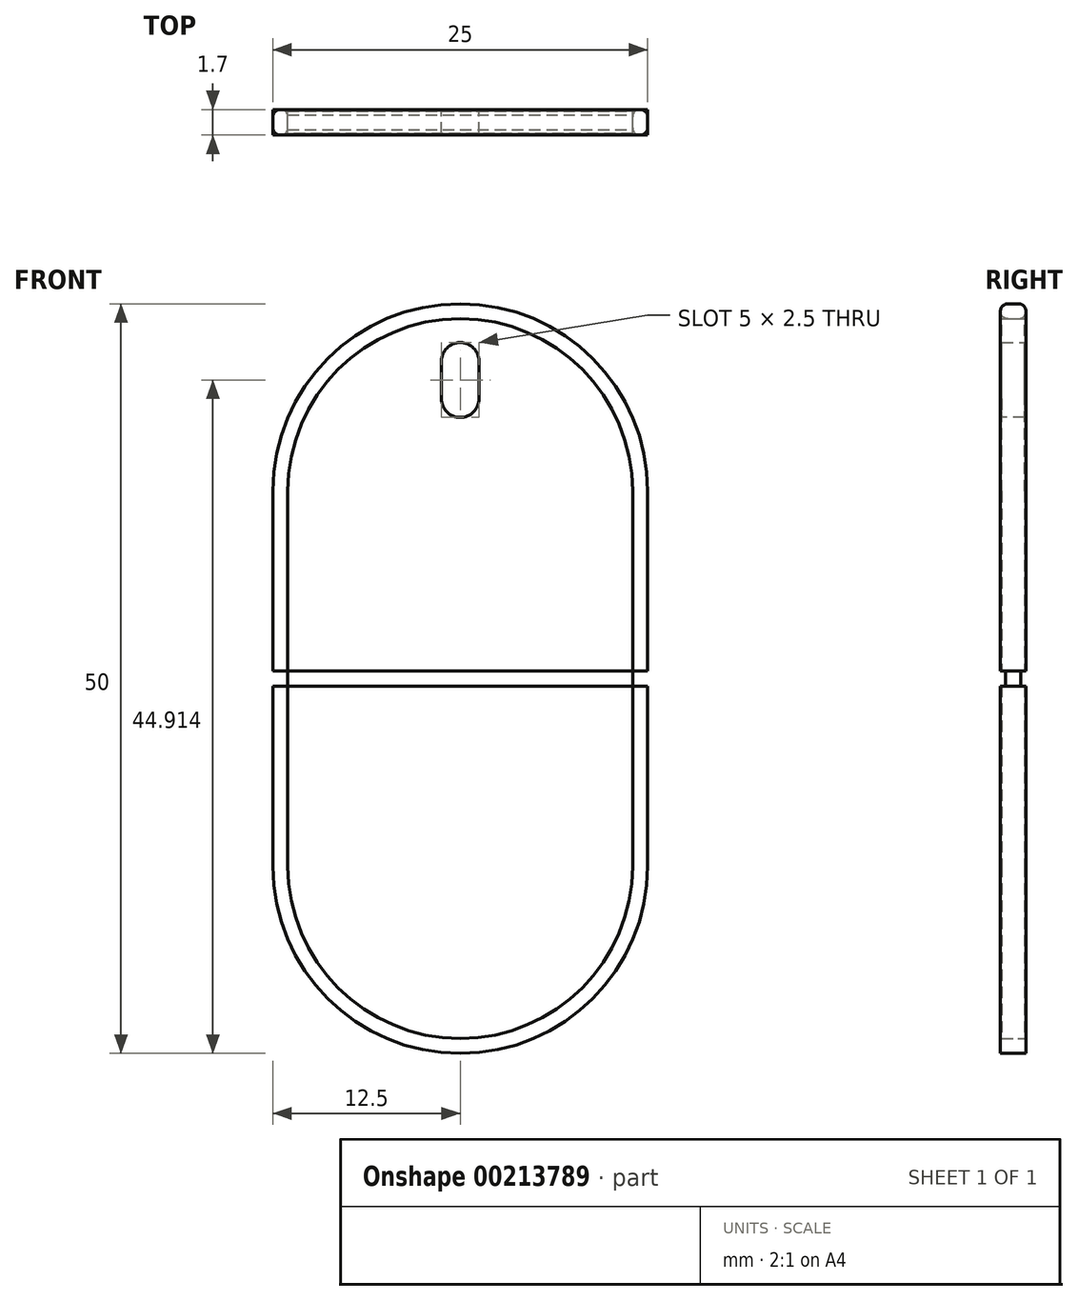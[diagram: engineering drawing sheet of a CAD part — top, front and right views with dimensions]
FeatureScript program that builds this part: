
annotation { "Feature Type Name" : "Feature", "Feature Type Description" : "" }
export const myFeature = defineFeature(function(context is Context, id is Id, definition is map)
    precondition{}
    {
        {
            var Q0;
            Q0=qCreatedBy(makeId("Front.planeOp"),FACE);
            var sketch = newSketch(context, id + "F0", { "sketchPlane" : qUnion([Q0])});
            skLineSegment(sketch, "E0.bottom", {"start": v(12.5, 25) * mm, "end": v(-12.5, 25) * mm});
            skLineSegment(sketch, "E0.top", {"start": v(12.5, -25) * mm, "end": v(-12.5, -25) * mm});
            skLineSegment(sketch, "E0.left", {"start": v(12.5, 25) * mm, "end": v(12.5, -25) * mm});
            skLineSegment(sketch, "E0.right", {"start": v(-12.5, 25) * mm, "end": v(-12.5, -25) * mm});
            skPoint(sketch, "E0.middle", {"position": v(0, 0) * mm});
            skLineSegment(sketch, "E1", {"start": v(-12.5, 0) * mm, "end": v(12.5, 0) * mm, "construction": true});
            skLineSegment(sketch, "E2.0", {"start": v(-12.5, 0.5) * mm, "end": v(12.5, 0.5) * mm});
            skLineSegment(sketch, "E3.MirrorCS", {"start": v(-12.5, -0.5) * mm, "end": v(12.5, -0.5) * mm});
            skLineSegment(sketch, "E4", {"start": v(11.5, 0.5) * mm, "end": v(11.5, -0.5) * mm});
            skLineSegment(sketch, "E5.MirrorCS", {"start": v(-11.5, 0.5) * mm, "end": v(-11.5, -0.5) * mm});
            skLineSegment(sketch, "E6.bottom", {"start": v(1.25, 17.41) * mm, "end": v(-1.25, 17.41) * mm});
            skLineSegment(sketch, "E6.top", {"start": v(1.25, 22.41) * mm, "end": v(-1.25, 22.41) * mm});
            skLineSegment(sketch, "E6.left", {"start": v(1.25, 17.41) * mm, "end": v(1.25, 22.41) * mm});
            skLineSegment(sketch, "E6.right", {"start": v(-1.25, 17.41) * mm, "end": v(-1.25, 22.41) * mm});
            skPoint(sketch, "E6.middle", {"position": v(0, 19.91) * mm});
            skLineSegment(sketch, "E7.0", {"start": v(0, 24) * mm, "end": v(0, 24) * mm});
            skLineSegment(sketch, "E7.1", {"start": v(11.5, 12.5) * mm, "end": v(11.5, -12.5) * mm});
            skLineSegment(sketch, "E7.2", {"start": v(0, -24) * mm, "end": v(0, -24) * mm});
            skLineSegment(sketch, "E7.3", {"start": v(-11.5, 12.5) * mm, "end": v(-11.5, -12.5) * mm});
            skPoint(sketch, "E8.visualSharp", {"position": v(11.5, 24) * mm});
            skArc(sketch, "E8.filletArc", {"start": v(11.5, 12.5) * mm, "mid": v(8.13, 20.63) * mm, "end": v(0, 24) * mm});
            skPoint(sketch, "E9.visualSharp", {"position": v(-11.5, 24) * mm});
            skArc(sketch, "E9.filletArc", {"start": v(0, 24) * mm, "mid": v(-8.13, 20.63) * mm, "end": v(-11.5, 12.5) * mm});
            skPoint(sketch, "E10.visualSharp", {"position": v(11.5, -24) * mm});
            skArc(sketch, "E10.filletArc", {"start": v(0, -24) * mm, "mid": v(8.13, -20.63) * mm, "end": v(11.5, -12.5) * mm});
            skPoint(sketch, "E11.visualSharp", {"position": v(-11.5, -24) * mm});
            skArc(sketch, "E11.filletArc", {"start": v(-11.5, -12.5) * mm, "mid": v(-8.13, -20.63) * mm, "end": v(0, -24) * mm});
            skSolve(sketch);
        }
        {
            var Q0;
            {var subQ7=sQuery(id+"F0.wireOp",EDGE,"E0.bottom");Q0=makeQuery(id+"F0.imprint","IMPRINT",FACE,{"disambiguationData":[TD([[makeQuery(id+"F0.imprint","IMPRINT",EDGE,{"derivedFrom":subQ7}),1.0]])]});}
            var Q1;
            {var subQ5=sQuery(id+"F0.wireOp",EDGE,"E0.top");Q1=makeQuery(id+"F0.imprint","IMPRINT",FACE,{"disambiguationData":[TD([[makeQuery(id+"F0.imprint","IMPRINT",EDGE,{"derivedFrom":subQ5}),-1.0]])]});}
            var Q2;
            {var subQ5=sQuery(id+"F0.wireOp",EDGE,"E7.2");Q2=makeQuery(id+"F0.imprint","IMPRINT",FACE,{"disambiguationData":[TD([[makeQuery(id+"F0.imprint","IMPRINT",EDGE,{"derivedFrom":subQ5}),-1.0]])]});}
            extrude(context, id + "F1", {"entities" : qUnion([Q0, Q1, Q2]), "depth" : .85 * mm, "hasSecondDirection" : true, "secondDirectionOppositeDirection" : true, "secondDirectionDepth" : .85 * mm});
        }
        {
            var Q0;
            Q0=makeQuery(id+"F1.opExtrude","SWEPT_EDGE",EDGE,{"disambiguationData":[OSD([sQuery(id+"F0.wireOp",EDGE,"E0.top"),sQuery(id+"F0.wireOp",EDGE,"E0.left")])]});
            var Q1;
            Q1=makeQuery(id+"F1.opExtrude","SWEPT_EDGE",EDGE,{"disambiguationData":[OSD([sQuery(id+"F0.wireOp",EDGE,"E0.top"),sQuery(id+"F0.wireOp",EDGE,"E0.right")])]});
            var Q2;
            Q2=makeQuery(id+"F1.opExtrude","SWEPT_EDGE",EDGE,{"disambiguationData":[OSD([sQuery(id+"F0.wireOp",EDGE,"E0.bottom"),sQuery(id+"F0.wireOp",EDGE,"E0.left")])]});
            var Q3;
            Q3=makeQuery(id+"F1.opExtrude","SWEPT_EDGE",EDGE,{"disambiguationData":[OSD([sQuery(id+"F0.wireOp",EDGE,"E0.bottom"),sQuery(id+"F0.wireOp",EDGE,"E0.right")])]});
            fillet(context, id + "F2", {"entities" : qUnion([Q0, Q1, Q2, Q3]), "radius" : 12.5 * mm, "tangentPropagation" : true, "allowEdgeOverflow" : false});
        }
        {
            var Q0;
            {var subQ4=sQuery(id+"F0.wireOp",EDGE,"E4");Q0=makeQuery(id+"F0.imprint","IMPRINT",FACE,{"disambiguationData":[TD([[makeQuery(id+"F0.imprint","IMPRINT",EDGE,{"derivedFrom":subQ4}),-1.0]])]});}
            extrude(context, id + "F3", {"entities" : qUnion([Q0]), "depth" : .5 * mm, "hasSecondDirection" : true, "secondDirectionOppositeDirection" : true, "secondDirectionDepth" : .5 * mm});
        }
        {
            var Q0;
            Q0=makeQuery(id+"F0.imprint","IMPRINT",FACE,{"disambiguationData":[TD([[makeQuery(id+"F0.imprint","IMPRINT",EDGE,{"derivedFrom":sQuery(id+"F0.wireOp",EDGE,"E6.bottom")}),1.0]])]});
            var Q1;
            {var subQ6=sQuery(id+"F0.wireOp",EDGE,"E10.filletArc");Q1=makeQuery(id+"F0.imprint","IMPRINT",FACE,{"disambiguationData":[TD([[makeQuery(id+"F0.imprint","IMPRINT",EDGE,{"derivedFrom":subQ6}),1.0]])]});}
            extrude(context, id + "F4", {"entities" : qUnion([Q0, Q1]), "depth" : .75 * mm, "hasSecondDirection" : true, "secondDirectionOppositeDirection" : true, "secondDirectionDepth" : .75 * mm});
        }
        {
            var Q0;
            Q0=makeQuery(id+"F4.opExtrude","SWEPT_EDGE",EDGE,{"disambiguationData":[OSD([sQuery(id+"F0.wireOp",EDGE,"E6.top"),sQuery(id+"F0.wireOp",EDGE,"E6.right")])]});
            var Q1;
            Q1=makeQuery(id+"F4.opExtrude","SWEPT_EDGE",EDGE,{"disambiguationData":[OSD([sQuery(id+"F0.wireOp",EDGE,"E6.top"),sQuery(id+"F0.wireOp",EDGE,"E6.left")])]});
            var Q2;
            Q2=makeQuery(id+"F4.opExtrude","SWEPT_EDGE",EDGE,{"disambiguationData":[OSD([sQuery(id+"F0.wireOp",EDGE,"E6.bottom"),sQuery(id+"F0.wireOp",EDGE,"E6.right")])]});
            var Q3;
            Q3=makeQuery(id+"F4.opExtrude","SWEPT_EDGE",EDGE,{"disambiguationData":[OSD([sQuery(id+"F0.wireOp",EDGE,"E6.bottom"),sQuery(id+"F0.wireOp",EDGE,"E6.left")])]});
            fillet(context, id + "F5", {"entities" : qUnion([Q0, Q1, Q2, Q3]), "radius" : 1.25 * mm, "tangentPropagation" : true, "allowEdgeOverflow" : false});
        }
        {
            var Q0;
            {var subQ0=sQuery(id+"F0.wireOp",EDGE,"E0.left");var subQ1=sQuery(id+"F0.wireOp",EDGE,"E0.bottom");Q0=makeQuery(id+"F2.opFillet","BLEND_EDGE",EDGE,{"blendedFrom":[makeQuery(id+"F1.opExtrude","SWEPT_EDGE",EDGE,{"disambiguationData":[OSD([subQ1,subQ0])]}),makeQuery(id+"F1.opExtrude","CAP_FACE",FACE,{"disambiguationData":[OSD([subQ1,subQ0,sQuery(id+"F0.wireOp",EDGE,"E0.right"),sQuery(id+"F0.wireOp",EDGE,"E2.0"),sQuery(id+"F0.wireOp",EDGE,"E7.1"),sQuery(id+"F0.wireOp",EDGE,"E7.3"),sQuery(id+"F0.wireOp",EDGE,"E8.filletArc"),sQuery(id+"F0.wireOp",EDGE,"E9.filletArc")])],"isStart":false})],"blendedInto":[makeQuery(id+"F1.opExtrude","CAP_FACE",FACE,{"disambiguationData":[OSD([subQ1,subQ0,sQuery(id+"F0.wireOp",EDGE,"E0.right"),sQuery(id+"F0.wireOp",EDGE,"E2.0"),sQuery(id+"F0.wireOp",EDGE,"E7.1"),sQuery(id+"F0.wireOp",EDGE,"E7.3"),sQuery(id+"F0.wireOp",EDGE,"E8.filletArc"),sQuery(id+"F0.wireOp",EDGE,"E9.filletArc")])],"isStart":false})]});}
            var Q1;
            {var subQ0=sQuery(id+"F0.wireOp",EDGE,"E0.left");Q1=makeQuery(id+"F1.opExtrude","CAP_EDGE",EDGE,{"disambiguationData":[OSD([subQ0]),TDD([makeQuery(id+"F0.imprint","IMPRINT",EDGE,{"disambiguationData":[TD([[makeQuery(id+"F0.imprint","INTERSECT",VERTEX,{"derivedFrom":[sQuery(id+"F0.wireOp",EDGE,"E0.bottom"),subQ0]}),-1.0]])],"derivedFrom":subQ0})])],"isStart":false});}
            var Q2;
            {var subQ0=sQuery(id+"F0.wireOp",EDGE,"E0.left");Q2=makeQuery(id+"F1.opExtrude","CAP_EDGE",EDGE,{"disambiguationData":[OSD([subQ0]),TDD([makeQuery(id+"F0.imprint","IMPRINT",EDGE,{"disambiguationData":[TD([[makeQuery(id+"F0.imprint","INTERSECT",VERTEX,{"derivedFrom":[sQuery(id+"F0.wireOp",EDGE,"E0.bottom"),subQ0]}),-1.0]])],"derivedFrom":subQ0})])],"isStart":true});}
            var Q3;
            {var subQ0=sQuery(id+"F0.wireOp",EDGE,"E0.left");var subQ1=sQuery(id+"F0.wireOp",EDGE,"E0.bottom");Q3=makeQuery(id+"F2.opFillet","BLEND_EDGE",EDGE,{"blendedFrom":[makeQuery(id+"F1.opExtrude","SWEPT_EDGE",EDGE,{"disambiguationData":[OSD([subQ1,subQ0])]}),makeQuery(id+"F1.opExtrude","CAP_FACE",FACE,{"disambiguationData":[OSD([subQ1,subQ0,sQuery(id+"F0.wireOp",EDGE,"E0.right"),sQuery(id+"F0.wireOp",EDGE,"E2.0"),sQuery(id+"F0.wireOp",EDGE,"E7.1"),sQuery(id+"F0.wireOp",EDGE,"E7.3"),sQuery(id+"F0.wireOp",EDGE,"E8.filletArc"),sQuery(id+"F0.wireOp",EDGE,"E9.filletArc")])],"isStart":true})],"blendedInto":[makeQuery(id+"F1.opExtrude","CAP_FACE",FACE,{"disambiguationData":[OSD([subQ1,subQ0,sQuery(id+"F0.wireOp",EDGE,"E0.right"),sQuery(id+"F0.wireOp",EDGE,"E2.0"),sQuery(id+"F0.wireOp",EDGE,"E7.1"),sQuery(id+"F0.wireOp",EDGE,"E7.3"),sQuery(id+"F0.wireOp",EDGE,"E8.filletArc"),sQuery(id+"F0.wireOp",EDGE,"E9.filletArc")])],"isStart":true})]});}
            var Q4;
            {var subQ0=sQuery(id+"F0.wireOp",EDGE,"E0.right");Q4=makeQuery(id+"F1.opExtrude","CAP_EDGE",EDGE,{"disambiguationData":[OSD([subQ0]),TDD([makeQuery(id+"F0.imprint","IMPRINT",EDGE,{"disambiguationData":[TD([[makeQuery(id+"F0.imprint","INTERSECT",VERTEX,{"derivedFrom":[sQuery(id+"F0.wireOp",EDGE,"E0.bottom"),subQ0]}),-1.0]])],"derivedFrom":subQ0})])],"isStart":false});}
            var Q5;
            {var subQ0=sQuery(id+"F0.wireOp",EDGE,"E0.right");Q5=makeQuery(id+"F1.opExtrude","CAP_EDGE",EDGE,{"disambiguationData":[OSD([subQ0]),TDD([makeQuery(id+"F0.imprint","IMPRINT",EDGE,{"disambiguationData":[TD([[makeQuery(id+"F0.imprint","INTERSECT",VERTEX,{"derivedFrom":[sQuery(id+"F0.wireOp",EDGE,"E0.bottom"),subQ0]}),-1.0]])],"derivedFrom":subQ0})])],"isStart":true});}
            var Q6;
            {var subQ0=sQuery(id+"F0.wireOp",EDGE,"E7.3");Q6=makeQuery(id+"F1.opExtrude","CAP_EDGE",EDGE,{"disambiguationData":[OSD([subQ0]),TDD([makeQuery(id+"F0.imprint","IMPRINT",EDGE,{"disambiguationData":[TD([[makeQuery(id+"F0.imprint","INTERSECT",VERTEX,{"derivedFrom":[subQ0,sQuery(id+"F0.wireOp",EDGE,"E9.filletArc")]}),-1.0]])],"derivedFrom":subQ0})])],"isStart":false});}
            var Q7;
            Q7=makeQuery(id+"F1.opExtrude","CAP_EDGE",EDGE,{"disambiguationData":[OSD([sQuery(id+"F0.wireOp",EDGE,"E8.filletArc"),sQuery(id+"F0.wireOp",EDGE,"E9.filletArc")])],"isStart":false});
            var Q8;
            {var subQ0=sQuery(id+"F0.wireOp",EDGE,"E7.1");Q8=makeQuery(id+"F1.opExtrude","CAP_EDGE",EDGE,{"disambiguationData":[OSD([subQ0]),TDD([makeQuery(id+"F0.imprint","IMPRINT",EDGE,{"disambiguationData":[TD([[makeQuery(id+"F0.imprint","INTERSECT",VERTEX,{"derivedFrom":[subQ0,sQuery(id+"F0.wireOp",EDGE,"E8.filletArc")]}),-1.0]])],"derivedFrom":subQ0})])],"isStart":true});}
            var Q9;
            Q9=makeQuery(id+"F1.opExtrude","CAP_EDGE",EDGE,{"disambiguationData":[OSD([sQuery(id+"F0.wireOp",EDGE,"E8.filletArc"),sQuery(id+"F0.wireOp",EDGE,"E9.filletArc")])],"isStart":true});
            var Q10;
            {var subQ0=sQuery(id+"F0.wireOp",EDGE,"E7.3");Q10=makeQuery(id+"F1.opExtrude","CAP_EDGE",EDGE,{"disambiguationData":[OSD([subQ0]),TDD([makeQuery(id+"F0.imprint","IMPRINT",EDGE,{"disambiguationData":[TD([[makeQuery(id+"F0.imprint","INTERSECT",VERTEX,{"derivedFrom":[subQ0,sQuery(id+"F0.wireOp",EDGE,"E9.filletArc")]}),-1.0]])],"derivedFrom":subQ0})])],"isStart":true});}
            var Q11;
            {var subQ0=sQuery(id+"F0.wireOp",EDGE,"E7.1");Q11=makeQuery(id+"F1.opExtrude","CAP_EDGE",EDGE,{"disambiguationData":[OSD([subQ0]),TDD([makeQuery(id+"F0.imprint","IMPRINT",EDGE,{"disambiguationData":[TD([[makeQuery(id+"F0.imprint","INTERSECT",VERTEX,{"derivedFrom":[subQ0,sQuery(id+"F0.wireOp",EDGE,"E8.filletArc")]}),-1.0]])],"derivedFrom":subQ0})])],"isStart":false});}
            fillet(context, id + "F6", {"entities" : qUnion([Q0, Q1, Q2, Q3, Q4, Q5, Q6, Q7, Q8, Q9, Q10, Q11]), "radius" : .5 * mm, "tangentPropagation" : true, "allowEdgeOverflow" : false});
        }
    });
